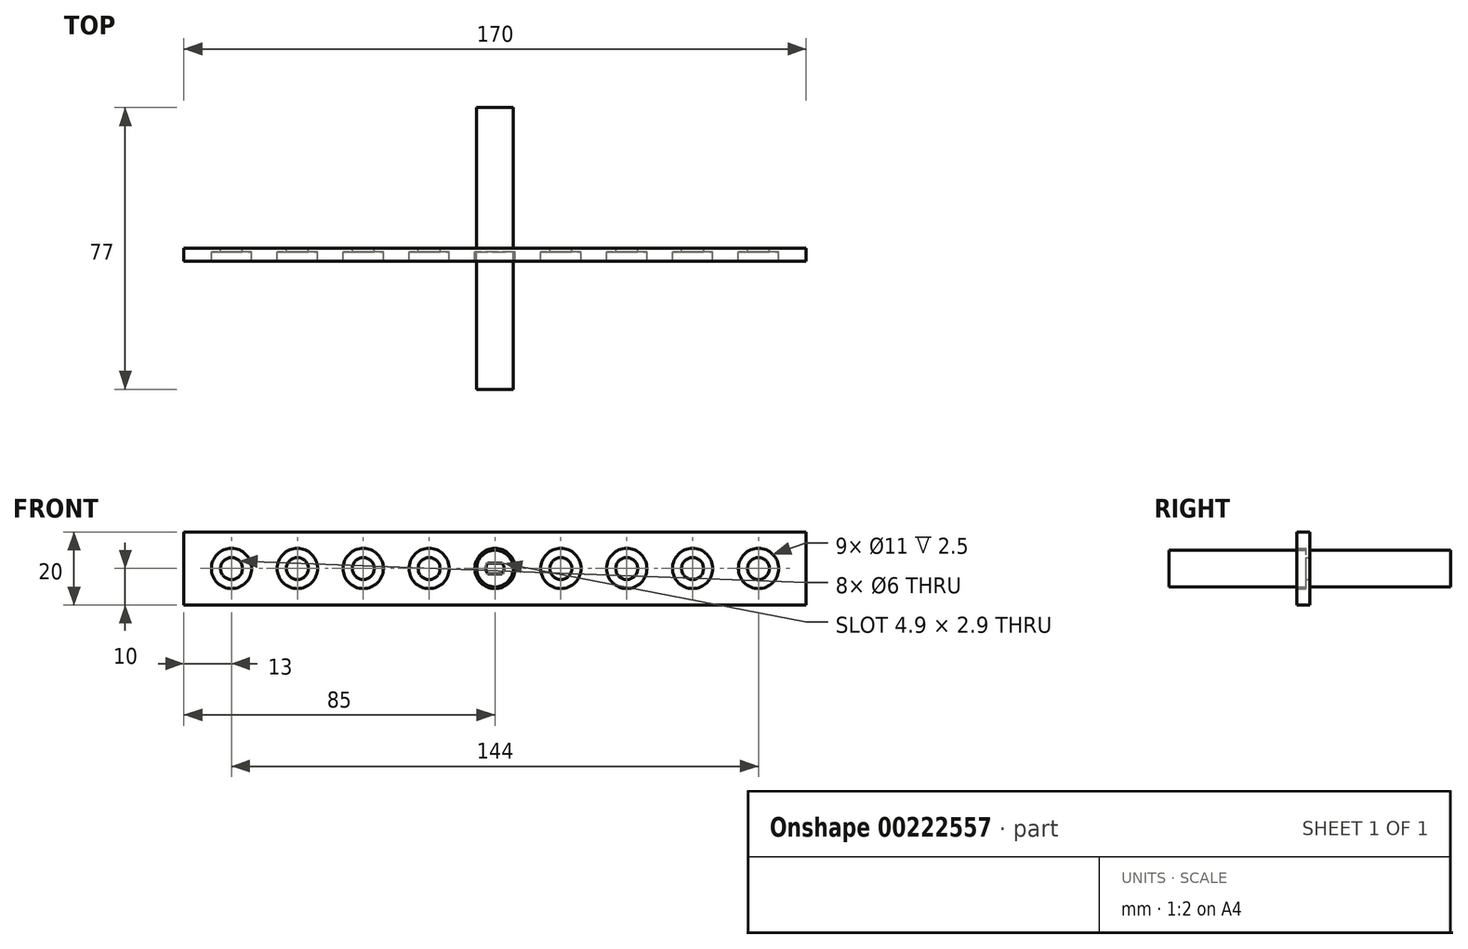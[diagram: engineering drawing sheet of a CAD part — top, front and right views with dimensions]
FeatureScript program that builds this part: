
annotation { "Feature Type Name" : "Feature", "Feature Type Description" : "" }
export const myFeature = defineFeature(function(context is Context, id is Id, definition is map)
    precondition{}
    {
        {
            var Q0;
            Q0=qCreatedBy(makeId("Front.planeOp"),FACE);
            var sketch = newSketch(context, id + "F0", { "sketchPlane" : qUnion([Q0])});
            skCircle(sketch, "E0", {"center": v(0, 0) * mm, "radius": 5 * mm});
            skArc(sketch, "E1", {"start": v(-1.97, 1.45) * mm, "mid": v(-2.45, 0) * mm, "end": v(-1.97, -1.45) * mm});
            skLineSegment(sketch, "E2.bottom", {"start": v(1.97, -1.45) * mm, "end": v(-1.97, -1.45) * mm});
            skLineSegment(sketch, "E2.top", {"start": v(1.97, 1.45) * mm, "end": v(-1.97, 1.45) * mm});
            skArc(sketch, "E3.trimOffspring", {"start": v(1.97, -1.45) * mm, "mid": v(2.45, 0) * mm, "end": v(1.97, 1.45) * mm});
            skSolve(sketch);
        }
        {
            var Q0;
            Q0=makeQuery(id+"F0.imprint","IMPRINT",FACE,{"disambiguationData":[TD([[makeQuery(id+"F0.imprint","IMPRINT",EDGE,{"derivedFrom":sQuery(id+"F0.wireOp",EDGE,"E0")}),1.0]])]});
            extrude(context, id + "F1", {"entities" : qUnion([Q0]), "endBound" : BoundingType.SYMMETRIC, "depth" : 77 * mm});
        }
        {
            var Q0;
            Q0=qCreatedBy(makeId("Front.planeOp"),FACE);
            var sketch = newSketch(context, id + "F2", { "sketchPlane" : qUnion([Q0])});
            skLineSegment(sketch, "E4.bottom", {"start": v(-85, 10) * mm, "end": v(85, 10) * mm});
            skLineSegment(sketch, "E4.top", {"start": v(-85, -10) * mm, "end": v(85, -10) * mm});
            skLineSegment(sketch, "E4.left", {"start": v(-85, 10) * mm, "end": v(-85, -10) * mm});
            skLineSegment(sketch, "E4.right", {"start": v(85, 10) * mm, "end": v(85, -10) * mm});
            skLineSegment(sketch, "E5", {"start": v(0, 10) * mm, "end": v(0, -10) * mm, "construction": true});
            skPoint(sketch, "E6", {"position": v(0, 0) * mm});
            skCircle(sketch, "E7", {"center": v(-72, 0) * mm, "radius": 5.5 * mm});
            skLineSegment(sketch, "E8", {"start": v(-85, 0) * mm, "end": v(85, 0) * mm, "construction": true});
            skLineSegment(sketch, "E9.direction1", {"start": v(-72, 0) * mm, "end": v(-57, 0) * mm, "construction": true});
            skCircle(sketch, "E10", {"center": v(-72, 0) * mm, "radius": 3 * mm});
            skCircle(sketch, "E11.1.0.0", {"center": v(-54, 0) * mm, "radius": 3 * mm});
            skCircle(sketch, "E11.1.0.1", {"center": v(-54, 0) * mm, "radius": 5.5 * mm});
            skCircle(sketch, "E11.2.0.0", {"center": v(-36, 0) * mm, "radius": 3 * mm});
            skCircle(sketch, "E11.2.0.1", {"center": v(-36, 0) * mm, "radius": 5.5 * mm});
            skCircle(sketch, "E11.3.0.0", {"center": v(-18, 0) * mm, "radius": 3 * mm});
            skCircle(sketch, "E11.3.0.1", {"center": v(-18, 0) * mm, "radius": 5.5 * mm});
            skCircle(sketch, "E11.4.0.0", {"center": v(0, 0) * mm, "radius": 3 * mm});
            skCircle(sketch, "E11.4.0.1", {"center": v(0, 0) * mm, "radius": 5.5 * mm});
            skCircle(sketch, "E11.5.0.0", {"center": v(18, 0) * mm, "radius": 3 * mm});
            skCircle(sketch, "E11.5.0.1", {"center": v(18, 0) * mm, "radius": 5.5 * mm});
            skCircle(sketch, "E11.6.0.0", {"center": v(36, 0) * mm, "radius": 3 * mm});
            skCircle(sketch, "E11.6.0.1", {"center": v(36, 0) * mm, "radius": 5.5 * mm});
            skCircle(sketch, "E11.7.0.0", {"center": v(54, 0) * mm, "radius": 3 * mm});
            skCircle(sketch, "E11.7.0.1", {"center": v(54, 0) * mm, "radius": 5.5 * mm});
            skCircle(sketch, "E11.8.0.0", {"center": v(72, 0) * mm, "radius": 3 * mm});
            skCircle(sketch, "E11.8.0.1", {"center": v(72, 0) * mm, "radius": 5.5 * mm});
            skLineSegment(sketch, "E11.direction1", {"start": v(-72, 0) * mm, "end": v(-54, 0) * mm, "construction": true});
            skSolve(sketch);
        }
        {
            var Q0;
            Q0=makeQuery(id+"F2.imprint","IMPRINT",FACE,{"disambiguationData":[TD([[makeQuery(id+"F2.imprint","IMPRINT",EDGE,{"derivedFrom":sQuery(id+"F2.wireOp",EDGE,"E4.bottom")}),-1.0]])]});
            extrude(context, id + "F3", {"entities" : qUnion([Q0]), "depth" : 3.5 * mm});
        }
        {
            var Q0;
            Q0=makeQuery(id+"F2.imprint","IMPRINT",FACE,{"disambiguationData":[TD([[makeQuery(id+"F2.imprint","IMPRINT",EDGE,{"derivedFrom":sQuery(id+"F2.wireOp",EDGE,"E7")}),1.0]])]});
            var Q1;
            Q1=makeQuery(id+"F2.imprint","IMPRINT",FACE,{"disambiguationData":[TD([[makeQuery(id+"F2.imprint","IMPRINT",EDGE,{"derivedFrom":sQuery(id+"F2.wireOp",EDGE,"E11.1.0.0")}),-1.0]])]});
            var Q2;
            Q2=makeQuery(id+"F2.imprint","IMPRINT",FACE,{"disambiguationData":[TD([[makeQuery(id+"F2.imprint","IMPRINT",EDGE,{"derivedFrom":sQuery(id+"F2.wireOp",EDGE,"E11.2.0.0")}),-1.0]])]});
            var Q3;
            Q3=makeQuery(id+"F2.imprint","IMPRINT",FACE,{"disambiguationData":[TD([[makeQuery(id+"F2.imprint","IMPRINT",EDGE,{"derivedFrom":sQuery(id+"F2.wireOp",EDGE,"E11.3.0.0")}),-1.0]])]});
            var Q4;
            Q4=makeQuery(id+"F2.imprint","IMPRINT",FACE,{"disambiguationData":[TD([[makeQuery(id+"F2.imprint","IMPRINT",EDGE,{"derivedFrom":sQuery(id+"F2.wireOp",EDGE,"E11.4.0.0")}),-1.0]])]});
            var Q5;
            Q5=makeQuery(id+"F2.imprint","IMPRINT",FACE,{"disambiguationData":[TD([[makeQuery(id+"F2.imprint","IMPRINT",EDGE,{"derivedFrom":sQuery(id+"F2.wireOp",EDGE,"E11.5.0.0")}),-1.0]])]});
            var Q6;
            Q6=makeQuery(id+"F2.imprint","IMPRINT",FACE,{"disambiguationData":[TD([[makeQuery(id+"F2.imprint","IMPRINT",EDGE,{"derivedFrom":sQuery(id+"F2.wireOp",EDGE,"E11.6.0.0")}),-1.0]])]});
            var Q7;
            Q7=makeQuery(id+"F2.imprint","IMPRINT",FACE,{"disambiguationData":[TD([[makeQuery(id+"F2.imprint","IMPRINT",EDGE,{"derivedFrom":sQuery(id+"F2.wireOp",EDGE,"E11.7.0.0")}),-1.0]])]});
            var Q8;
            Q8=makeQuery(id+"F2.imprint","IMPRINT",FACE,{"disambiguationData":[TD([[makeQuery(id+"F2.imprint","IMPRINT",EDGE,{"derivedFrom":sQuery(id+"F2.wireOp",EDGE,"E11.8.0.0")}),-1.0]])]});
            extrude(context, id + "F4", {"entities" : qUnion([Q0, Q1, Q2, Q3, Q4, Q5, Q6, Q7, Q8]), "operationType" : NewBodyOperationType.ADD, "depth" : 1 * mm});
        }
    });
